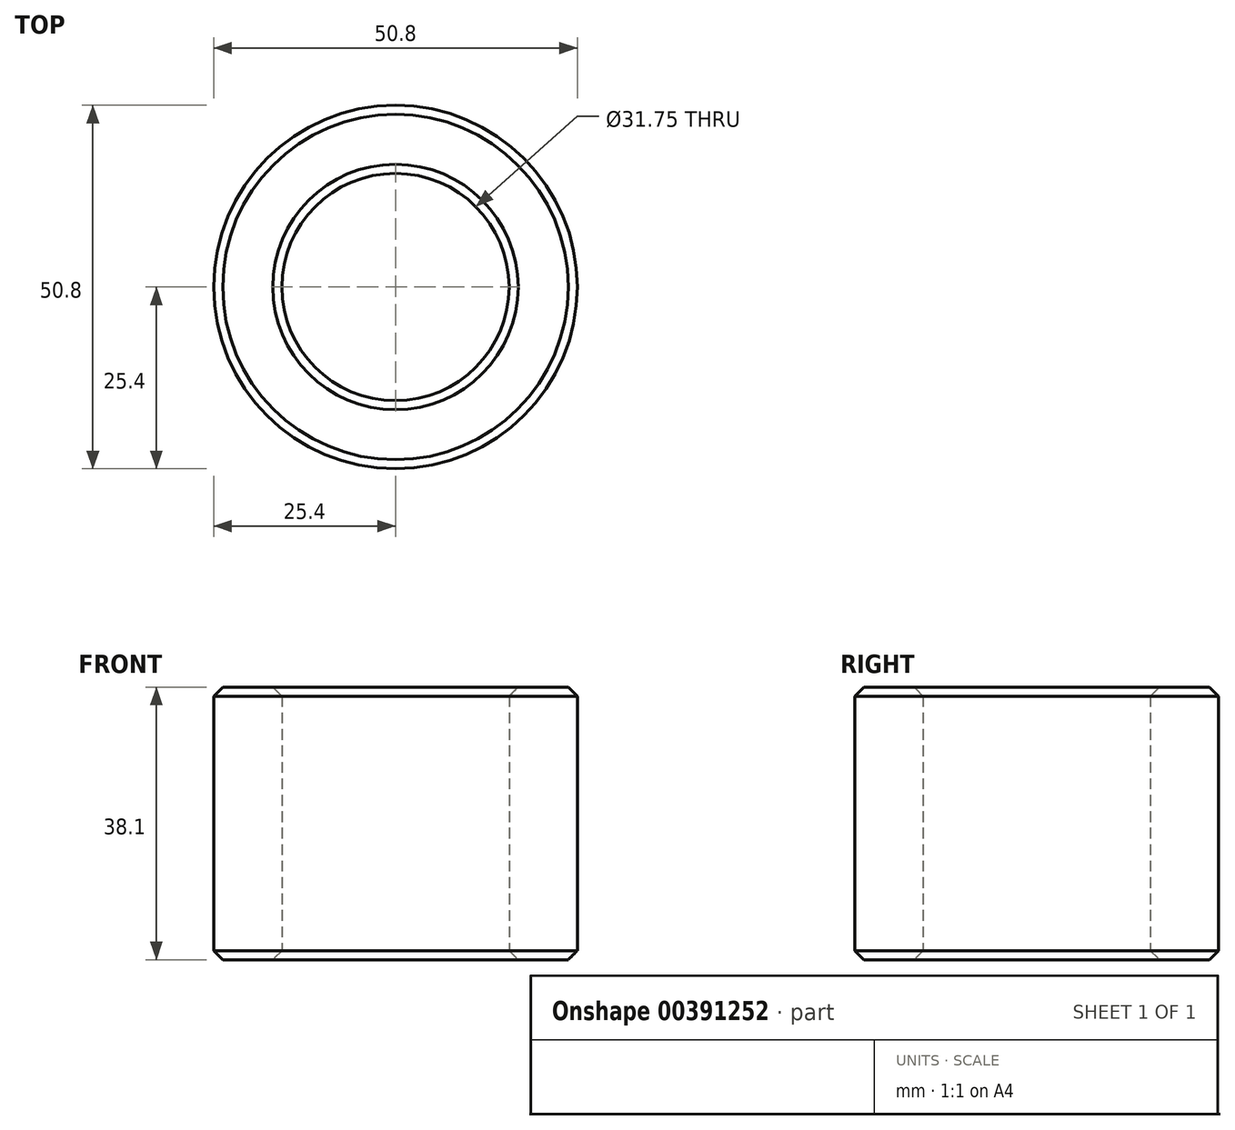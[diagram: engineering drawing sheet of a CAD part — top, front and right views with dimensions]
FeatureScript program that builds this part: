
annotation { "Feature Type Name" : "Feature", "Feature Type Description" : "" }
export const myFeature = defineFeature(function(context is Context, id is Id, definition is map)
    precondition{}
    {
        {
            var Q0;
            Q0=qCreatedBy(makeId("Front.planeOp"),FACE);
            var sketch = newSketch(context, id + "F0", { "sketchPlane" : qUnion([Q0])});
            skLineSegment(sketch, "E0", {"start": v(-25.4, 0) * mm, "end": v(-15.88, 0) * mm});
            skLineSegment(sketch, "E1", {"start": v(-25.4, 38.1) * mm, "end": v(-15.88, 38.1) * mm});
            skLineSegment(sketch, "E2", {"start": v(-15.88, 38.1) * mm, "end": v(-15.88, 0) * mm});
            skLineSegment(sketch, "E3.0", {"start": v(-25.4, 38.1) * mm, "end": v(-25.4, 0) * mm});
            skLineSegment(sketch, "E4", {"start": v(0, 0) * mm, "end": v(0, 51.44) * mm});
            skSolve(sketch);
        }
        {
            var Q0;
            Q0=makeQuery(id+"F0.imprint","IMPRINT",FACE,{"disambiguationData":[TD([[makeQuery(id+"F0.imprint","IMPRINT",EDGE,{"derivedFrom":sQuery(id+"F0.wireOp",EDGE,"E0")}),1.0]])]});
            var Q1;
            Q1=sQuery(id+"F0.wireOp",EDGE,"E4");
            revolve(context, id + "F1", {"entities" : qUnion([Q0]), "axis" : qUnion([Q1]), "revolveType" : RevolveType.FULL});
        }
        {
            var Q0;
            Q0=makeQuery(id+"F1.opRevolve","SWEPT_EDGE",EDGE,{"disambiguationData":[OSD([sQuery(id+"F0.wireOp",EDGE,"E1"),sQuery(id+"F0.wireOp",EDGE,"E2")])]});
            var Q1;
            Q1=makeQuery(id+"F1.opRevolve","SWEPT_EDGE",EDGE,{"disambiguationData":[OSD([sQuery(id+"F0.wireOp",EDGE,"E0"),sQuery(id+"F0.wireOp",EDGE,"E2")])]});
            chamfer(context, id + "F2", {"entities" : qUnion([Q0, Q1]), "width" : 1.27 * mm, "tangentPropagation" : true});
        }
        {
            var Q0;
            Q0=makeQuery(id+"F1.opRevolve","SWEPT_EDGE",EDGE,{"disambiguationData":[OSD([sQuery(id+"F0.wireOp",EDGE,"E1"),sQuery(id+"F0.wireOp",EDGE,"E3.0")])]});
            var Q1;
            Q1=makeQuery(id+"F1.opRevolve","SWEPT_EDGE",EDGE,{"disambiguationData":[OSD([sQuery(id+"F0.wireOp",EDGE,"E0"),sQuery(id+"F0.wireOp",EDGE,"E3.0")])]});
            chamfer(context, id + "F3", {"entities" : qUnion([Q0, Q1]), "width" : 1.27 * mm, "tangentPropagation" : true});
        }
    });
